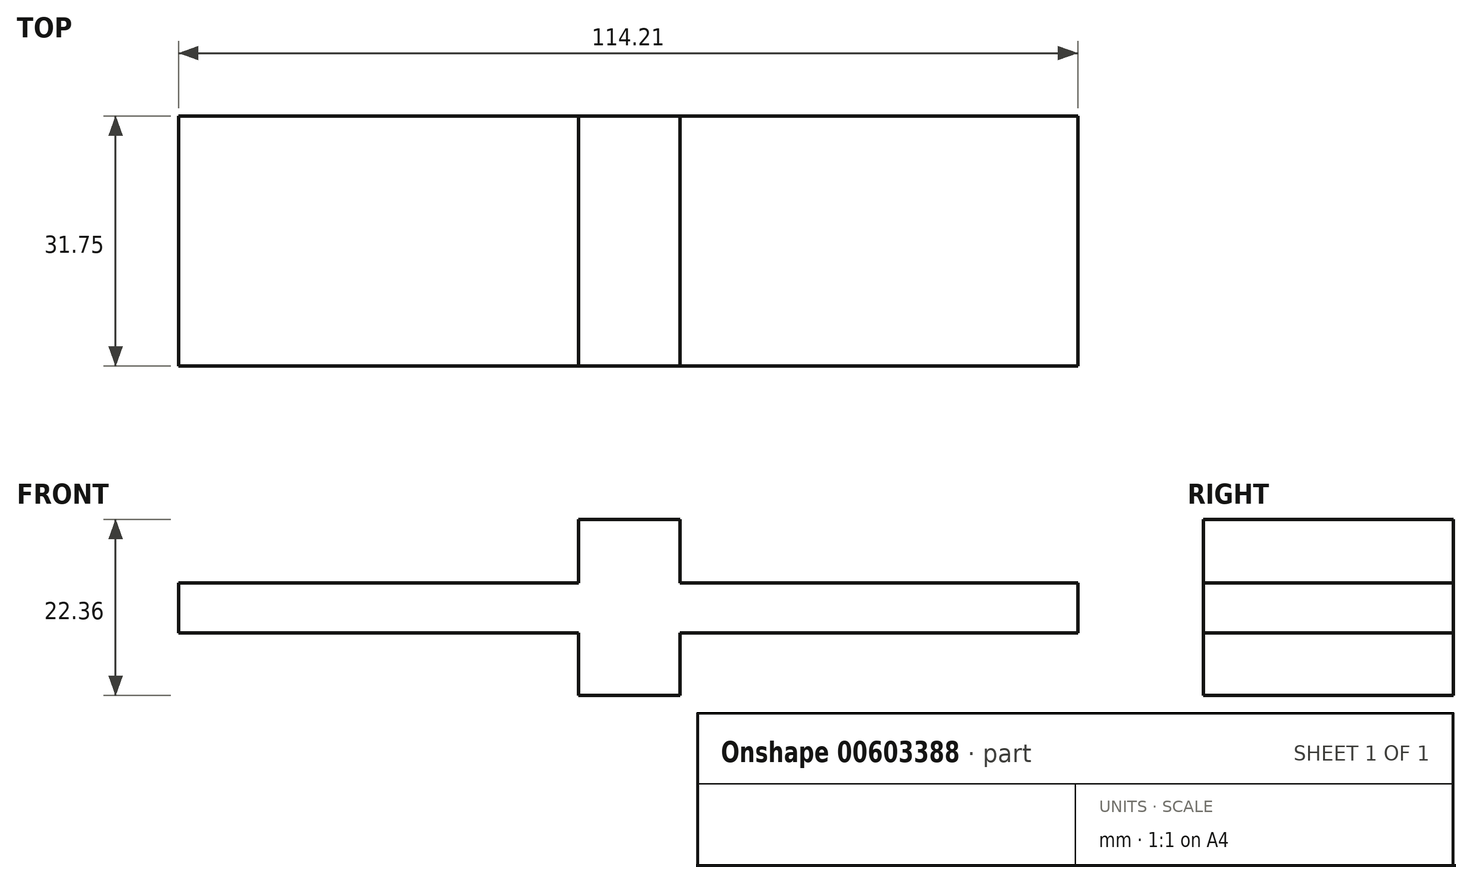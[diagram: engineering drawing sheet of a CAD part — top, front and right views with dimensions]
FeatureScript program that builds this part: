
annotation { "Feature Type Name" : "Feature", "Feature Type Description" : "" }
export const myFeature = defineFeature(function(context is Context, id is Id, definition is map)
    precondition{}
    {
        {
            var Q0;
            Q0=qCreatedBy(makeId("Front.planeOp"),FACE);
            var sketch = newSketch(context, id + "F0", { "sketchPlane" : qUnion([Q0])});
            skLineSegment(sketch, "E0", {"start": v(0, 0) * mm, "end": v(50.8, 0) * mm});
            skLineSegment(sketch, "E1", {"start": v(50.8, 0) * mm, "end": v(50.8, 8.08) * mm});
            skLineSegment(sketch, "E2", {"start": v(50.8, 8.08) * mm, "end": v(63.67, 8.08) * mm});
            skLineSegment(sketch, "E3", {"start": v(63.67, 8.08) * mm, "end": v(63.67, 0) * mm});
            skLineSegment(sketch, "E4", {"start": v(63.67, 0) * mm, "end": v(114.2, 0) * mm});
            skLineSegment(sketch, "E5", {"start": v(114.2, 0) * mm, "end": v(114.2, -6.31) * mm});
            skLineSegment(sketch, "E6", {"start": v(114.2, -6.31) * mm, "end": v(63.67, -6.31) * mm});
            skLineSegment(sketch, "E7", {"start": v(63.67, -6.31) * mm, "end": v(63.67, -14.28) * mm});
            skLineSegment(sketch, "E8", {"start": v(63.67, -14.28) * mm, "end": v(50.8, -14.28) * mm});
            skLineSegment(sketch, "E9", {"start": v(50.8, -14.28) * mm, "end": v(50.8, -6.31) * mm});
            skLineSegment(sketch, "E10", {"start": v(50.8, -6.31) * mm, "end": v(0, -6.31) * mm});
            skLineSegment(sketch, "E11", {"start": v(0, -6.31) * mm, "end": v(0, 0) * mm});
            skSolve(sketch);
        }
        {
            var Q0;
            Q0 = qSketchRegion(id + "F0", true);
            extrude(context, id + "F1", {"entities" : qUnion([Q0]), "depth" : 31.75 * mm, "offsetDistance" : 25.4 * mm});
        }
    });
